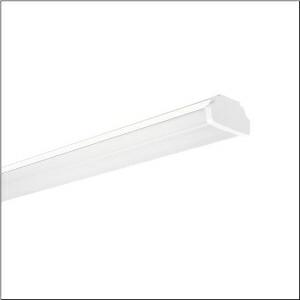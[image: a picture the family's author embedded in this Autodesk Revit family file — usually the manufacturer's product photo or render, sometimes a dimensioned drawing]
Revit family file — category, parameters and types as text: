
# Revit family: modario_r__31_mo_53bm811d2v4085_981c
name_source: partatom
category: Lighting Fixtures
units: mm (PartAtom-declared; Revit-internal decimal feet)

## family parameters
Cut with Voids When Loaded = No
Host = Face
Light Source = No
Part Type = Normal
Room Calculation Point = No
Round Connector Dimension = Use Diameter
Shared = No

## types (1)
- --- (1 x LED, 8930 lm, 61.8 W, 4000K)
    Apparent Load = 62 VA
    CIE Flux Codes = 52 78 94 90 100
    Color Rendering = 80
    Color Temperature = 4000K
    Default Elevation = 1800 mm
    Description = Modario® 31 MOluminaire insert, length: 1.495mm, width: 81mm, height: 82mm, LED rated luminous flux: 8.930lm, light colour: 840, control gear: DALI 2, control gear: ECG DALI, with plug, 5-pole, with phase selection, mains connection: 220..240V, AC, 50/60Hz, primary optical cover: cover, of PMMA, light emission: direct distribution, primary light characteristic: symmetric, protection rating (complete): IP20, protection rating (LED compartment): IP50, insulation class (complete): insulation class I (protective earthing), certification: CE, ENEC, VDE, UKCA, permissible ambient temperature for indoor applications: -25..+30°C, corresponds to IFS (International Featured Standards) requirements for safety and quality in the food industry, reducing of maximum allowable ambient temperature of 5°C with ceiling mounting, packaging unit: 1 piece
    Height = 92 mm
    Lamp = 1 x LED
    Lamp Light Flux = 8930 lm
    Lamp Power = 61.8 W
    Lamp count = 1
    Length = 1495 mm
    Luminous efficacy = 145 lm/W
    Manufacturer = Siteco
    ModVariant = No
    Model = 53BM811D2V4085
    Mounting Place = Ceiling
    Mounting Type = Pendant
    Number of Poles = 1
    OnlyDefault = Yes
    Power Factor = 1
    Product Name = Modario® 31 MO
    Product group = luminaire insert
    ProductGroupID = 902
    Protection Class = Protection class I
    Protection Degree = IP 20
    RLX_Detail_Level = 1
    RlxData = <blob elided: 41973 chars, md5=8f3f2470>
    Socket = socket
    Standby Power = 0 W
    System Light Flux = 8930 lm
    System Power = 62 W
    Type Comments = factory setting: luminous flux: 100 % | dim-lin: 254 | 500 mA
    Type Image = l_1003447.jpg
    URL = http://relux.com
    VarID = @adj_117501
    Voltage = 0 V
    Weight = 0.00 kg
    Width = 81 mm

## geometry (parser evidence)
native form markers: Blend x4, Sweep x12
no freeform markers — native parametric forms only
